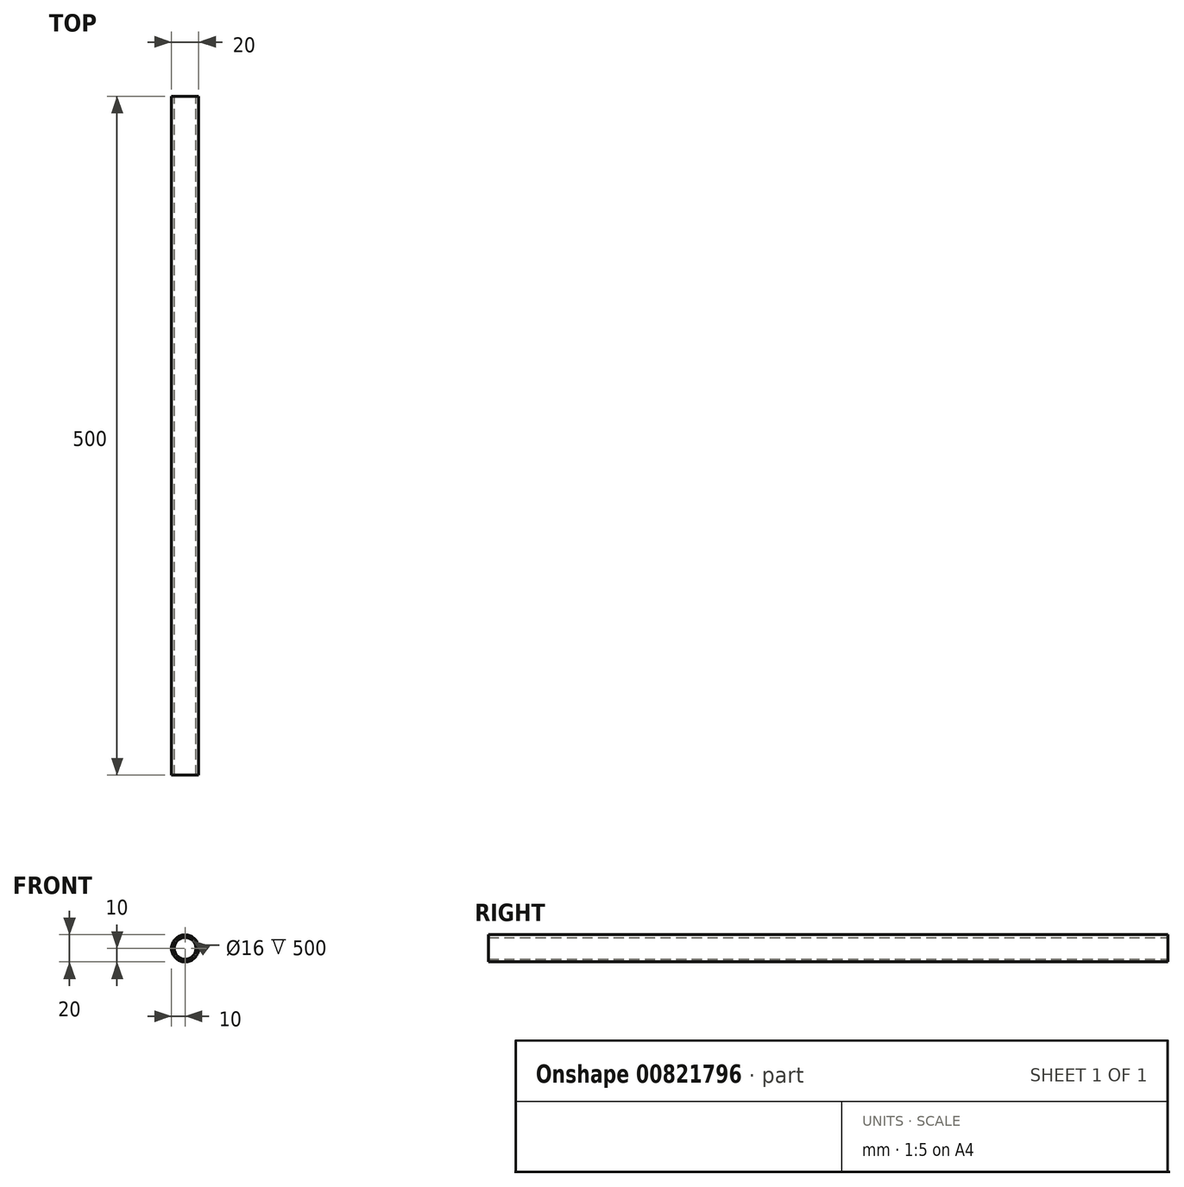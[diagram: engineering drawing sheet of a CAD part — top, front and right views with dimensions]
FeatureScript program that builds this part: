
annotation { "Feature Type Name" : "Feature", "Feature Type Description" : "" }
export const myFeature = defineFeature(function(context is Context, id is Id, definition is map)
    precondition{}
    {
        {
            var Q0;
            Q0=qCreatedBy(makeId("Front.planeOp"),FACE);
            var sketch = newSketch(context, id + "F0", { "sketchPlane" : qUnion([Q0])});
            skCircle(sketch, "E0", {"center": v(0, 0) * mm, "radius": 10 * mm});
            skCircle(sketch, "E1", {"center": v(0, 0) * mm, "radius": 8 * mm});
            skSolve(sketch);
        }
        {
            assignVariable(context, id + "F1", {"name" : "y_alu_rod_length", "anyValue" : 500});
        }
        {
            var Q0;
            Q0=makeQuery(id+"F0.imprint","IMPRINT",FACE,{"disambiguationData":[TD([[makeQuery(id+"F0.imprint","IMPRINT",EDGE,{"derivedFrom":sQuery(id+"F0.wireOp",EDGE,"E0")}),1.0]])]});
            extrude(context, id + "F2", {"entities" : qUnion([Q0]), "depth" : (getVariable(context, 'y_alu_rod_length')) * mm, "offsetDistance" : 25 * mm});
        }
        {
            var Q0;
            Q0=makeQuery(id+"F2.opExtrude","CAP_FACE",FACE,{"disambiguationData":[OSD([sQuery(id+"F0.wireOp",EDGE,"E0"),sQuery(id+"F0.wireOp",EDGE,"E1")])],"isStart":true});
            var sketch = newSketch(context, id + "F3", { "sketchPlane" : qUnion([Q0])});
            skLineSegment(sketch, "E2", {"start": v(0, 0) * mm, "end": v(43.18, 0) * mm, "construction": true});
            skLineSegment(sketch, "E3", {"start": v(0, 0) * mm, "end": v(0, 53.69) * mm, "construction": true});
            skSolve(sketch);
        }
    });
